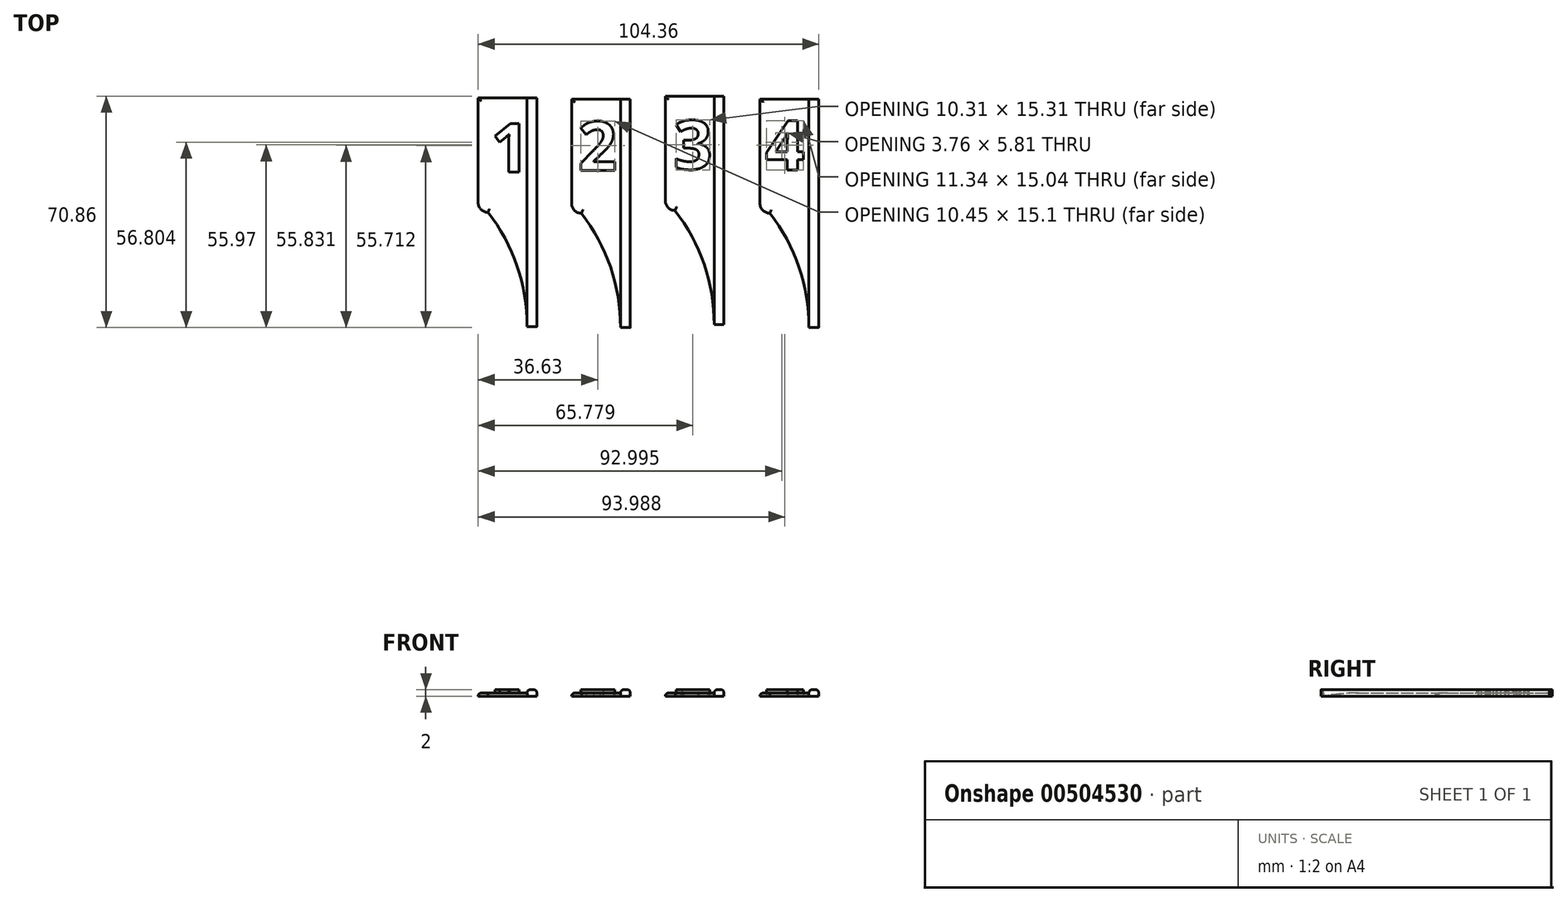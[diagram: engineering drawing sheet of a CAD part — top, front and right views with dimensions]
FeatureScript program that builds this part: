
annotation { "Feature Type Name" : "Feature", "Feature Type Description" : "" }
export const myFeature = defineFeature(function(context is Context, id is Id, definition is map)
    precondition{}
    {
        {
            var Q0;
            Q0=qCreatedBy(makeId("Top.planeOp"),FACE);
            var sketch = newSketch(context, id + "F0", { "sketchPlane" : qUnion([Q0])});
            skLineSegment(sketch, "E0.bottom", {"start": v(-42.45, -18.74) * mm, "end": v(-30.45, -18.74) * mm});
            skLineSegment(sketch, "E0.top", {"start": v(-45.45, 16.26) * mm, "end": v(-30.45, 16.26) * mm});
            skLineSegment(sketch, "E0.left", {"start": v(-45.45, -15.74) * mm, "end": v(-45.45, 16.26) * mm});
            skLineSegment(sketch, "E0.right", {"start": v(-30.45, -18.74) * mm, "end": v(-30.45, 16.26) * mm});
            skLineSegment(sketch, "E1.bottom", {"start": v(-30.45, 16.26) * mm, "end": v(-27.45, 16.26) * mm});
            skLineSegment(sketch, "E1.top", {"start": v(-30.45, -53.74) * mm, "end": v(-27.45, -53.74) * mm});
            skLineSegment(sketch, "E1.left", {"start": v(-30.45, 16.26) * mm, "end": v(-30.45, -53.74) * mm});
            skLineSegment(sketch, "E1.right", {"start": v(-27.45, 16.26) * mm, "end": v(-27.45, -53.74) * mm});
            skPoint(sketch, "E2.visualSharp", {"position": v(-45.45, -18.74) * mm});
            skArc(sketch, "E2.filletArc", {"start": v(-45.45, -15.74) * mm, "mid": v(-44.57, -17.86) * mm, "end": v(-42.45, -18.74) * mm});
            skArc(sketch, "E3", {"start": v(-30.45, -53.74) * mm, "mid": v(-33.53, -35.24) * mm, "end": v(-42.45, -18.74) * mm});
            skText(sketch, "E4", { "text": "1", "fontName": "OpenSans-Bold.ttf"});
            skLineSegment(sketch, "E5.bottom", {"start": v(-13.82, -19.04) * mm, "end": v(-1.82, -19.04) * mm});
            skLineSegment(sketch, "E5.top", {"start": v(-16.82, 15.96) * mm, "end": v(-1.82, 15.96) * mm});
            skLineSegment(sketch, "E5.left", {"start": v(-16.82, -16.04) * mm, "end": v(-16.82, 15.96) * mm});
            skLineSegment(sketch, "E5.right", {"start": v(-1.82, -19.04) * mm, "end": v(-1.82, 15.96) * mm});
            skLineSegment(sketch, "E6.bottom", {"start": v(-1.82, 15.96) * mm, "end": v(1.18, 15.96) * mm});
            skLineSegment(sketch, "E6.top", {"start": v(-1.82, -54.04) * mm, "end": v(1.18, -54.04) * mm});
            skLineSegment(sketch, "E6.left", {"start": v(-1.82, 15.96) * mm, "end": v(-1.82, -54.04) * mm});
            skLineSegment(sketch, "E6.right", {"start": v(1.18, 15.96) * mm, "end": v(1.18, -54.04) * mm});
            skPoint(sketch, "E7.visualSharp", {"position": v(-16.82, -19.04) * mm});
            skArc(sketch, "E7.filletArc", {"start": v(-16.82, -16.04) * mm, "mid": v(-15.94, -18.16) * mm, "end": v(-13.82, -19.04) * mm});
            skArc(sketch, "E8", {"start": v(-1.82, -54.04) * mm, "mid": v(-4.9, -35.54) * mm, "end": v(-13.82, -19.04) * mm});
            skText(sketch, "E9", { "text": "2", "fontName": "OpenSans-Bold.ttf"});
            skLineSegment(sketch, "E10.bottom", {"start": v(14.88, -18.18) * mm, "end": v(26.88, -18.18) * mm});
            skLineSegment(sketch, "E10.top", {"start": v(11.88, 16.82) * mm, "end": v(26.88, 16.82) * mm});
            skLineSegment(sketch, "E10.left", {"start": v(11.88, -15.18) * mm, "end": v(11.88, 16.82) * mm});
            skLineSegment(sketch, "E10.right", {"start": v(26.88, -18.18) * mm, "end": v(26.88, 16.82) * mm});
            skLineSegment(sketch, "E11.bottom", {"start": v(26.88, 16.82) * mm, "end": v(29.88, 16.82) * mm});
            skLineSegment(sketch, "E11.top", {"start": v(26.88, -53.18) * mm, "end": v(29.88, -53.18) * mm});
            skLineSegment(sketch, "E11.left", {"start": v(26.88, 16.82) * mm, "end": v(26.88, -53.18) * mm});
            skLineSegment(sketch, "E11.right", {"start": v(29.88, 16.82) * mm, "end": v(29.88, -53.18) * mm});
            skPoint(sketch, "E12.visualSharp", {"position": v(11.88, -18.18) * mm});
            skArc(sketch, "E12.filletArc", {"start": v(11.88, -15.18) * mm, "mid": v(12.76, -17.3) * mm, "end": v(14.88, -18.18) * mm});
            skArc(sketch, "E13", {"start": v(26.88, -53.18) * mm, "mid": v(23.8, -34.68) * mm, "end": v(14.88, -18.18) * mm});
            skLineSegment(sketch, "E14.bottom", {"start": v(43.91, -19.02) * mm, "end": v(55.91, -19.02) * mm});
            skLineSegment(sketch, "E14.top", {"start": v(40.91, 15.98) * mm, "end": v(55.91, 15.98) * mm});
            skLineSegment(sketch, "E14.left", {"start": v(40.91, -16.02) * mm, "end": v(40.91, 15.98) * mm});
            skLineSegment(sketch, "E14.right", {"start": v(55.91, -19.02) * mm, "end": v(55.91, 15.98) * mm});
            skLineSegment(sketch, "E15.bottom", {"start": v(55.91, 15.98) * mm, "end": v(58.91, 15.98) * mm});
            skLineSegment(sketch, "E15.top", {"start": v(55.91, -54.02) * mm, "end": v(58.91, -54.02) * mm});
            skLineSegment(sketch, "E15.left", {"start": v(55.91, 15.98) * mm, "end": v(55.91, -54.02) * mm});
            skLineSegment(sketch, "E15.right", {"start": v(58.91, 15.98) * mm, "end": v(58.91, -54.02) * mm});
            skPoint(sketch, "E16.visualSharp", {"position": v(40.91, -19.02) * mm});
            skArc(sketch, "E16.filletArc", {"start": v(40.91, -16.02) * mm, "mid": v(41.8, -18.14) * mm, "end": v(43.91, -19.02) * mm});
            skArc(sketch, "E17", {"start": v(55.91, -54.02) * mm, "mid": v(52.83, -35.52) * mm, "end": v(43.91, -19.02) * mm});
            skText(sketch, "E18", { "text": "3", "fontName": "OpenSans-Bold.ttf"});
            skText(sketch, "E19", { "text": "4", "fontName": "OpenSans-Bold.ttf"});
            const initialGuessF0  = {"E4": [-0.04157, -0.0064, 1, 0, 0.01502], "E9": [-0.01484, -0.00588, 1, 0, 0.01502], "E18": [0.01438, -0.00552, 1, 0, 0.01502], "E19": [0.04251, -0.00573, 1, 0, 0.01517]};
            skSetInitialGuess(sketch, initialGuessF0);
            skSolve(sketch);
        }
        {
            var Q0;
            {var subQ0=sQuery(id+"F0.wireOp",EDGE,"E0.bottom");Q0=makeQuery(id+"F0.imprint","IMPRINT",FACE,{"disambiguationData":[TD([[makeQuery(id+"F0.imprint","IMPRINT",EDGE,{"derivedFrom":subQ0}),1.0]])]});}
            extrude(context, id + "F1", {"entities" : qUnion([Q0]), "depth" : 1 * mm});
        }
        {
            var Q0;
            {var subQ3=sQuery(id+"F0.wireOp",EDGE,"E1.bottom");Q0=makeQuery(id+"F0.imprint","IMPRINT",FACE,{"disambiguationData":[TD([[makeQuery(id+"F0.imprint","IMPRINT",EDGE,{"derivedFrom":subQ3}),-1.0]])]});}
            extrude(context, id + "F2", {"entities" : qUnion([Q0]), "operationType" : NewBodyOperationType.ADD, "depth" : 2 * mm});
        }
        {
            var Q0;
            Q0=makeQuery(id+"F0.imprint","IMPRINT",FACE,{"disambiguationData":[TD([[makeQuery(id+"F0.imprint","IMPRINT",EDGE,{"derivedFrom":sQuery(id+"F0.wireOp",EDGE,"E4.sketch_text.stroke-0")}),-1.0]])]});
            extrude(context, id + "F3", {"entities" : qUnion([Q0]), "operationType" : NewBodyOperationType.ADD, "depth" : 2 * mm});
        }
        {
            var Q0;
            {var subQ0=sQuery(id+"F0.wireOp",EDGE,"E0.bottom");Q0=makeQuery(id+"F0.imprint","IMPRINT",FACE,{"disambiguationData":[TD([[makeQuery(id+"F0.imprint","IMPRINT",EDGE,{"derivedFrom":subQ0}),-1.0]])]});}
            extrude(context, id + "F4", {"entities" : qUnion([Q0]), "operationType" : NewBodyOperationType.ADD, "depth" : 1 * mm});
        }
        {
            var Q0;
            Q0=makeQuery(id+"F2.opExtrude","CAP_EDGE",EDGE,{"disambiguationData":[OSD([sQuery(id+"F0.wireOp",EDGE,"E1.right")])],"isStart":false});
            fillet(context, id + "F5", {"entities" : qUnion([Q0]), "radius" : 1 * mm, "tangentPropagation" : true, "allowEdgeOverflow" : false});
        }
        {
            var Q0;
            Q0=makeQuery(id+"F2.opExtrude","CAP_EDGE",EDGE,{"disambiguationData":[OSD([sQuery(id+"F0.wireOp",EDGE,"E1.left")])],"isStart":false});
            fillet(context, id + "F6", {"entities" : qUnion([Q0]), "radius" : 1 * mm, "tangentPropagation" : true, "allowEdgeOverflow" : false});
        }
        {
            var Q0;
            Q0=makeQuery(id+"F1.opExtrude","CAP_EDGE",EDGE,{"disambiguationData":[OSD([sQuery(id+"F0.wireOp",EDGE,"E2.filletArc")])],"isStart":false});
            var Q1;
            Q1=makeQuery(id+"F4.opExtrude","CAP_EDGE",EDGE,{"disambiguationData":[OSD([sQuery(id+"F0.wireOp",EDGE,"E3")])],"isStart":false});
            var Q2;
            Q2=makeQuery(id+"F1.opExtrude","CAP_EDGE",EDGE,{"disambiguationData":[OSD([sQuery(id+"F0.wireOp",EDGE,"E0.top")])],"isStart":false});
            var Q3;
            Q3=makeQuery(id+"F1.opExtrude","CAP_EDGE",EDGE,{"disambiguationData":[OSD([sQuery(id+"F0.wireOp",EDGE,"E0.left")])],"isStart":false});
            fillet(context, id + "F7", {"entities" : qUnion([Q0, Q1, Q2, Q3]), "radius" : 1 * mm, "tangentPropagation" : true, "allowEdgeOverflow" : false});
        }
        {
            var Q0;
            {var subQ2=sQuery(id+"F0.wireOp",EDGE,"E5.bottom");Q0=makeQuery(id+"F0.imprint","IMPRINT",FACE,{"disambiguationData":[TD([[makeQuery(id+"F0.imprint","IMPRINT",EDGE,{"derivedFrom":subQ2}),1.0]])]});}
            var Q1;
            {var subQ1=sQuery(id+"F0.wireOp",EDGE,"E10.bottom");Q1=makeQuery(id+"F0.imprint","IMPRINT",FACE,{"disambiguationData":[TD([[makeQuery(id+"F0.imprint","IMPRINT",EDGE,{"derivedFrom":subQ1}),1.0]])]});}
            var Q2;
            {var subQ0=sQuery(id+"F0.wireOp",EDGE,"E14.bottom");Q2=makeQuery(id+"F0.imprint","IMPRINT",FACE,{"disambiguationData":[TD([[makeQuery(id+"F0.imprint","IMPRINT",EDGE,{"derivedFrom":subQ0}),1.0]])]});}
            var Q3;
            {var subQ0=sQuery(id+"F0.wireOp",EDGE,"E14.bottom");Q3=makeQuery(id+"F0.imprint","IMPRINT",FACE,{"disambiguationData":[TD([[makeQuery(id+"F0.imprint","IMPRINT",EDGE,{"derivedFrom":subQ0}),-1.0]])]});}
            var Q4;
            {var subQ0=sQuery(id+"F0.wireOp",EDGE,"E10.bottom");Q4=makeQuery(id+"F0.imprint","IMPRINT",FACE,{"disambiguationData":[TD([[makeQuery(id+"F0.imprint","IMPRINT",EDGE,{"derivedFrom":subQ0}),-1.0]])]});}
            var Q5;
            {var subQ0=sQuery(id+"F0.wireOp",EDGE,"E5.bottom");Q5=makeQuery(id+"F0.imprint","IMPRINT",FACE,{"disambiguationData":[TD([[makeQuery(id+"F0.imprint","IMPRINT",EDGE,{"derivedFrom":subQ0}),-1.0]])]});}
            extrude(context, id + "F8", {"entities" : qUnion([Q0, Q1, Q2, Q3, Q4, Q5]), "depth" : 1 * mm});
        }
        {
            var Q0;
            Q0=makeQuery(id+"F0.imprint","IMPRINT",FACE,{"disambiguationData":[TD([[makeQuery(id+"F0.imprint","IMPRINT",EDGE,{"derivedFrom":sQuery(id+"F0.wireOp",EDGE,"E9.sketch_text.stroke-0")}),-1.0]])]});
            var Q1;
            Q1=makeQuery(id+"F0.imprint","IMPRINT",FACE,{"disambiguationData":[TD([[makeQuery(id+"F0.imprint","IMPRINT",EDGE,{"derivedFrom":sQuery(id+"F0.wireOp",EDGE,"E18.sketch_text.stroke-0")}),-1.0]])]});
            var Q2;
            Q2=makeQuery(id+"F0.imprint","IMPRINT",FACE,{"disambiguationData":[TD([[makeQuery(id+"F0.imprint","IMPRINT",EDGE,{"derivedFrom":sQuery(id+"F0.wireOp",EDGE,"E19.sketch_text.stroke-0")}),-1.0]])]});
            extrude(context, id + "F9", {"entities" : qUnion([Q0, Q1, Q2]), "depth" : 2 * mm});
        }
        {
            var Q0;
            {var subQ3=sQuery(id+"F0.wireOp",EDGE,"E6.bottom");Q0=makeQuery(id+"F0.imprint","IMPRINT",FACE,{"disambiguationData":[TD([[makeQuery(id+"F0.imprint","IMPRINT",EDGE,{"derivedFrom":subQ3}),-1.0]])]});}
            var Q1;
            {var subQ3=sQuery(id+"F0.wireOp",EDGE,"E11.bottom");Q1=makeQuery(id+"F0.imprint","IMPRINT",FACE,{"disambiguationData":[TD([[makeQuery(id+"F0.imprint","IMPRINT",EDGE,{"derivedFrom":subQ3}),-1.0]])]});}
            var Q2;
            {var subQ3=sQuery(id+"F0.wireOp",EDGE,"E15.bottom");Q2=makeQuery(id+"F0.imprint","IMPRINT",FACE,{"disambiguationData":[TD([[makeQuery(id+"F0.imprint","IMPRINT",EDGE,{"derivedFrom":subQ3}),-1.0]])]});}
            extrude(context, id + "F10", {"entities" : qUnion([Q0, Q1, Q2]), "depth" : 2 * mm});
        }
        {
            var Q0;
            Q0=makeQuery(id+"F8.opExtrude","CAP_EDGE",EDGE,{"disambiguationData":[OSD([sQuery(id+"F0.wireOp",EDGE,"E8")])],"isStart":false});
            var Q1;
            Q1=makeQuery(id+"F8.opExtrude","CAP_EDGE",EDGE,{"disambiguationData":[OSD([sQuery(id+"F0.wireOp",EDGE,"E7.filletArc")])],"isStart":false});
            var Q2;
            Q2=makeQuery(id+"F8.opExtrude","CAP_EDGE",EDGE,{"disambiguationData":[OSD([sQuery(id+"F0.wireOp",EDGE,"E5.top")])],"isStart":false});
            var Q3;
            Q3=makeQuery(id+"F8.opExtrude","CAP_EDGE",EDGE,{"disambiguationData":[OSD([sQuery(id+"F0.wireOp",EDGE,"E14.top")])],"isStart":false});
            var Q4;
            Q4=makeQuery(id+"F8.opExtrude","CAP_EDGE",EDGE,{"disambiguationData":[OSD([sQuery(id+"F0.wireOp",EDGE,"E5.left")])],"isStart":false});
            var Q5;
            Q5=makeQuery(id+"F8.opExtrude","CAP_EDGE",EDGE,{"disambiguationData":[OSD([sQuery(id+"F0.wireOp",EDGE,"E10.top")])],"isStart":false});
            var Q6;
            Q6=makeQuery(id+"F8.opExtrude","CAP_EDGE",EDGE,{"disambiguationData":[OSD([sQuery(id+"F0.wireOp",EDGE,"E10.left")])],"isStart":false});
            var Q7;
            Q7=makeQuery(id+"F8.opExtrude","CAP_EDGE",EDGE,{"disambiguationData":[OSD([sQuery(id+"F0.wireOp",EDGE,"E12.filletArc")])],"isStart":false});
            var Q8;
            Q8=makeQuery(id+"F8.opExtrude","CAP_EDGE",EDGE,{"disambiguationData":[OSD([sQuery(id+"F0.wireOp",EDGE,"E13")])],"isStart":false});
            var Q9;
            Q9=makeQuery(id+"F8.opExtrude","CAP_EDGE",EDGE,{"disambiguationData":[OSD([sQuery(id+"F0.wireOp",EDGE,"E14.left")])],"isStart":false});
            var Q10;
            Q10=makeQuery(id+"F8.opExtrude","CAP_EDGE",EDGE,{"disambiguationData":[OSD([sQuery(id+"F0.wireOp",EDGE,"E16.filletArc")])],"isStart":false});
            var Q11;
            Q11=makeQuery(id+"F8.opExtrude","CAP_EDGE",EDGE,{"disambiguationData":[OSD([sQuery(id+"F0.wireOp",EDGE,"E17")])],"isStart":false});
            fillet(context, id + "F11", {"entities" : qUnion([Q0, Q1, Q2, Q3, Q4, Q5, Q6, Q7, Q8, Q9, Q10, Q11]), "radius" : 1 * mm, "tangentPropagation" : true, "allowEdgeOverflow" : false});
        }
        {
            var Q0;
            Q0=makeQuery(id+"F10.opExtrude","CAP_EDGE",EDGE,{"disambiguationData":[OSD([sQuery(id+"F0.wireOp",EDGE,"E15.right")])],"isStart":false});
            var Q1;
            Q1=makeQuery(id+"F10.opExtrude","CAP_EDGE",EDGE,{"disambiguationData":[OSD([sQuery(id+"F0.wireOp",EDGE,"E15.left")])],"isStart":false});
            var Q2;
            Q2=makeQuery(id+"F10.opExtrude","CAP_EDGE",EDGE,{"disambiguationData":[OSD([sQuery(id+"F0.wireOp",EDGE,"E11.right")])],"isStart":false});
            var Q3;
            Q3=makeQuery(id+"F10.opExtrude","CAP_EDGE",EDGE,{"disambiguationData":[OSD([sQuery(id+"F0.wireOp",EDGE,"E6.right")])],"isStart":false});
            var Q4;
            Q4=makeQuery(id+"F10.opExtrude","CAP_EDGE",EDGE,{"disambiguationData":[OSD([sQuery(id+"F0.wireOp",EDGE,"E6.left")])],"isStart":false});
            fillet(context, id + "F12", {"entities" : qUnion([Q0, Q1, Q2, Q3, Q4]), "radius" : 1 * mm, "tangentPropagation" : true, "allowEdgeOverflow" : false});
        }
        {
            var Q0;
            Q0=makeQuery(id+"F10.opExtrude","CAP_EDGE",EDGE,{"disambiguationData":[OSD([sQuery(id+"F0.wireOp",EDGE,"E11.left")])],"isStart":false});
            fillet(context, id + "F13", {"entities" : qUnion([Q0]), "radius" : 1 * mm, "tangentPropagation" : true, "allowEdgeOverflow" : false});
        }
    });
